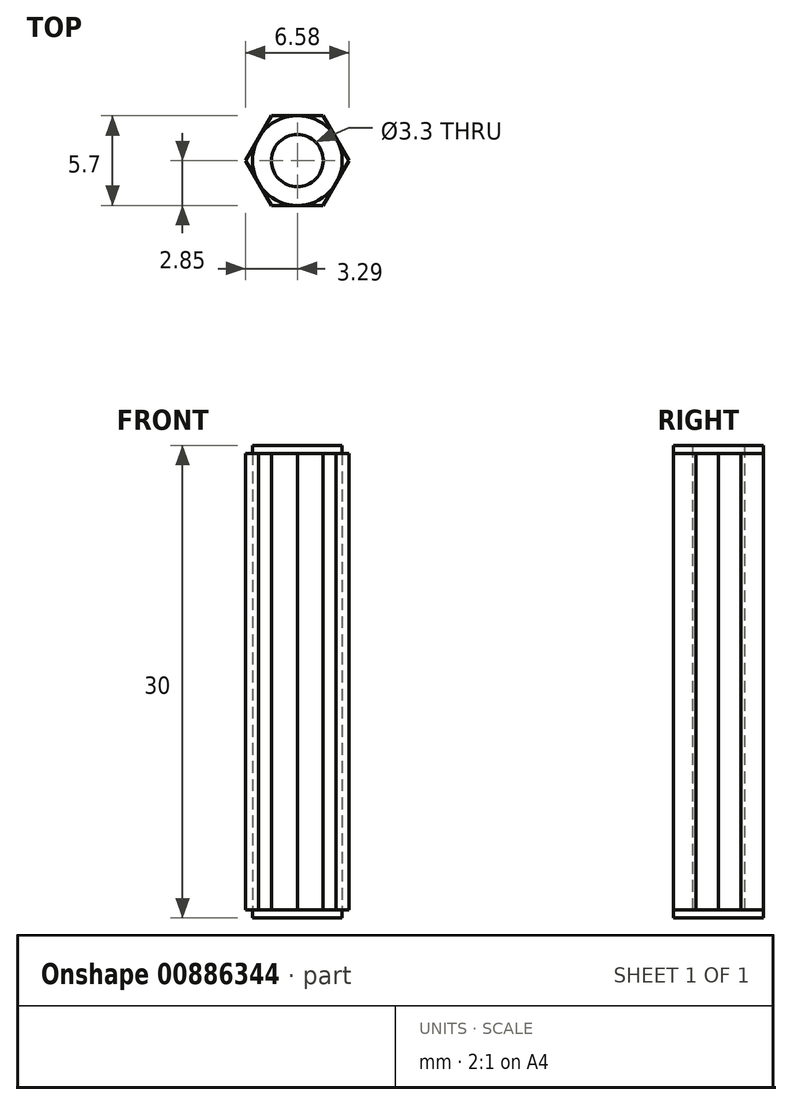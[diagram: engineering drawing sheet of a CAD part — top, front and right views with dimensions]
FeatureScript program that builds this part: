
annotation { "Feature Type Name" : "Feature", "Feature Type Description" : "" }
export const myFeature = defineFeature(function(context is Context, id is Id, definition is map)
    precondition{}
    {
        {
            var Q0;
            Q0=qCreatedBy(makeId("Top.planeOp"),FACE);
            var sketch = newSketch(context, id + "F0", { "sketchPlane" : qUnion([Q0])});
            skCircle(sketch, "E0.cCircle", {"center": v(0, 0) * mm, "radius": 2.85 * mm});
            skLineSegment(sketch, "E0.0", {"start": v(-1.65, 2.85) * mm, "end": v(1.65, 2.85) * mm});
            skLineSegment(sketch, "E0.1", {"start": v(1.65, 2.85) * mm, "end": v(3.3, 0) * mm});
            skLineSegment(sketch, "E0.2", {"start": v(3.3, 0) * mm, "end": v(1.65, -2.85) * mm});
            skLineSegment(sketch, "E0.3", {"start": v(1.65, -2.85) * mm, "end": v(-1.65, -2.85) * mm});
            skLineSegment(sketch, "E0.4", {"start": v(-1.65, -2.85) * mm, "end": v(-3.3, 0) * mm});
            skLineSegment(sketch, "E0.5", {"start": v(-3.3, 0) * mm, "end": v(-1.65, 2.85) * mm});
            skPoint(sketch, "E0.0.midPoint", {"position": v(0, 2.85) * mm});
            skCircle(sketch, "E1", {"center": v(0, 0) * mm, "radius": 1.65 * mm});
            skSolve(sketch);
        }
        {
            var Q0;
            Q0=sQuery(id+"F0.wireOp",EDGE,"E0.cCircle");
            extrude(context, id + "F1", {"bodyType" : ToolBodyType.SURFACE, "surfaceEntities" : qUnion([Q0]), "endBound" : BoundingType.SYMMETRIC, "depth" : 30 * mm, "offsetDistance" : 25 * mm});
        }
        {
            var Q0;
            {var subQ0=sQuery(id+"F0.wireOp",EDGE,"E0.5");var subQ1=sQuery(id+"F0.wireOp",EDGE,"E0.cCircle");var subQ2=makeQuery(id+"F0.imprint","INTERSECT",VERTEX,{"derivedFrom":[subQ1,subQ0]});Q0=makeQuery(id+"F0.imprint","IMPRINT",FACE,{"disambiguationData":[TD([[makeQuery(id+"F0.imprint","IMPRINT",EDGE,{"disambiguationData":[TD([[subQ2,-1.0]])],"derivedFrom":subQ1}),-1.0]])]});}
            var Q1;
            {var subQ0=sQuery(id+"F0.wireOp",EDGE,"E0.0");var subQ1=sQuery(id+"F0.wireOp",EDGE,"E0.cCircle");var subQ2=makeQuery(id+"F0.imprint","INTERSECT",VERTEX,{"derivedFrom":[subQ1,subQ0]});Q1=makeQuery(id+"F0.imprint","IMPRINT",FACE,{"disambiguationData":[TD([[makeQuery(id+"F0.imprint","IMPRINT",EDGE,{"disambiguationData":[TD([[subQ2,-1.0]])],"derivedFrom":subQ1}),-1.0]])]});}
            var Q2;
            {var subQ0=sQuery(id+"F0.wireOp",EDGE,"E0.0");var subQ1=sQuery(id+"F0.wireOp",EDGE,"E0.cCircle");var subQ2=makeQuery(id+"F0.imprint","INTERSECT",VERTEX,{"derivedFrom":[subQ1,subQ0]});Q2=makeQuery(id+"F0.imprint","IMPRINT",FACE,{"disambiguationData":[TD([[makeQuery(id+"F0.imprint","IMPRINT",EDGE,{"disambiguationData":[TD([[subQ2,1.0]])],"derivedFrom":subQ1}),-1.0]])]});}
            var Q3;
            {var subQ0=sQuery(id+"F0.wireOp",EDGE,"E0.1");var subQ1=sQuery(id+"F0.wireOp",EDGE,"E0.cCircle");var subQ2=makeQuery(id+"F0.imprint","INTERSECT",VERTEX,{"derivedFrom":[subQ1,subQ0]});Q3=makeQuery(id+"F0.imprint","IMPRINT",FACE,{"disambiguationData":[TD([[makeQuery(id+"F0.imprint","IMPRINT",EDGE,{"disambiguationData":[TD([[subQ2,1.0]])],"derivedFrom":subQ1}),-1.0]])]});}
            var Q4;
            {var subQ0=sQuery(id+"F0.wireOp",EDGE,"E0.3");var subQ1=sQuery(id+"F0.wireOp",EDGE,"E0.cCircle");var subQ2=makeQuery(id+"F0.imprint","INTERSECT",VERTEX,{"derivedFrom":[subQ1,subQ0]});Q4=makeQuery(id+"F0.imprint","IMPRINT",FACE,{"disambiguationData":[TD([[makeQuery(id+"F0.imprint","IMPRINT",EDGE,{"disambiguationData":[TD([[subQ2,-1.0]])],"derivedFrom":subQ1}),-1.0]])]});}
            var Q5;
            {var subQ0=sQuery(id+"F0.wireOp",EDGE,"E0.4");var subQ1=sQuery(id+"F0.wireOp",EDGE,"E0.cCircle");var subQ2=makeQuery(id+"F0.imprint","INTERSECT",VERTEX,{"derivedFrom":[subQ1,subQ0]});Q5=makeQuery(id+"F0.imprint","IMPRINT",FACE,{"disambiguationData":[TD([[makeQuery(id+"F0.imprint","IMPRINT",EDGE,{"disambiguationData":[TD([[subQ2,-1.0]])],"derivedFrom":subQ1}),-1.0]])]});}
            extrude(context, id + "F2", {"entities" : qUnion([Q0, Q1, Q2, Q3, Q4, Q5]), "endBound" : BoundingType.SYMMETRIC, "depth" : 29 * mm, "offsetDistance" : 25 * mm});
        }
        {
            var Q0;
            Q0=makeQuery(id+"F0.imprint","IMPRINT",FACE,{"disambiguationData":[TD([[makeQuery(id+"F0.imprint","IMPRINT",EDGE,{"derivedFrom":sQuery(id+"F0.wireOp",EDGE,"E1")}),-1.0]])]});
            extrude(context, id + "F3", {"entities" : qUnion([Q0]), "endBound" : BoundingType.SYMMETRIC, "depth" : 30 * mm, "offsetDistance" : 25 * mm});
        }
    });
